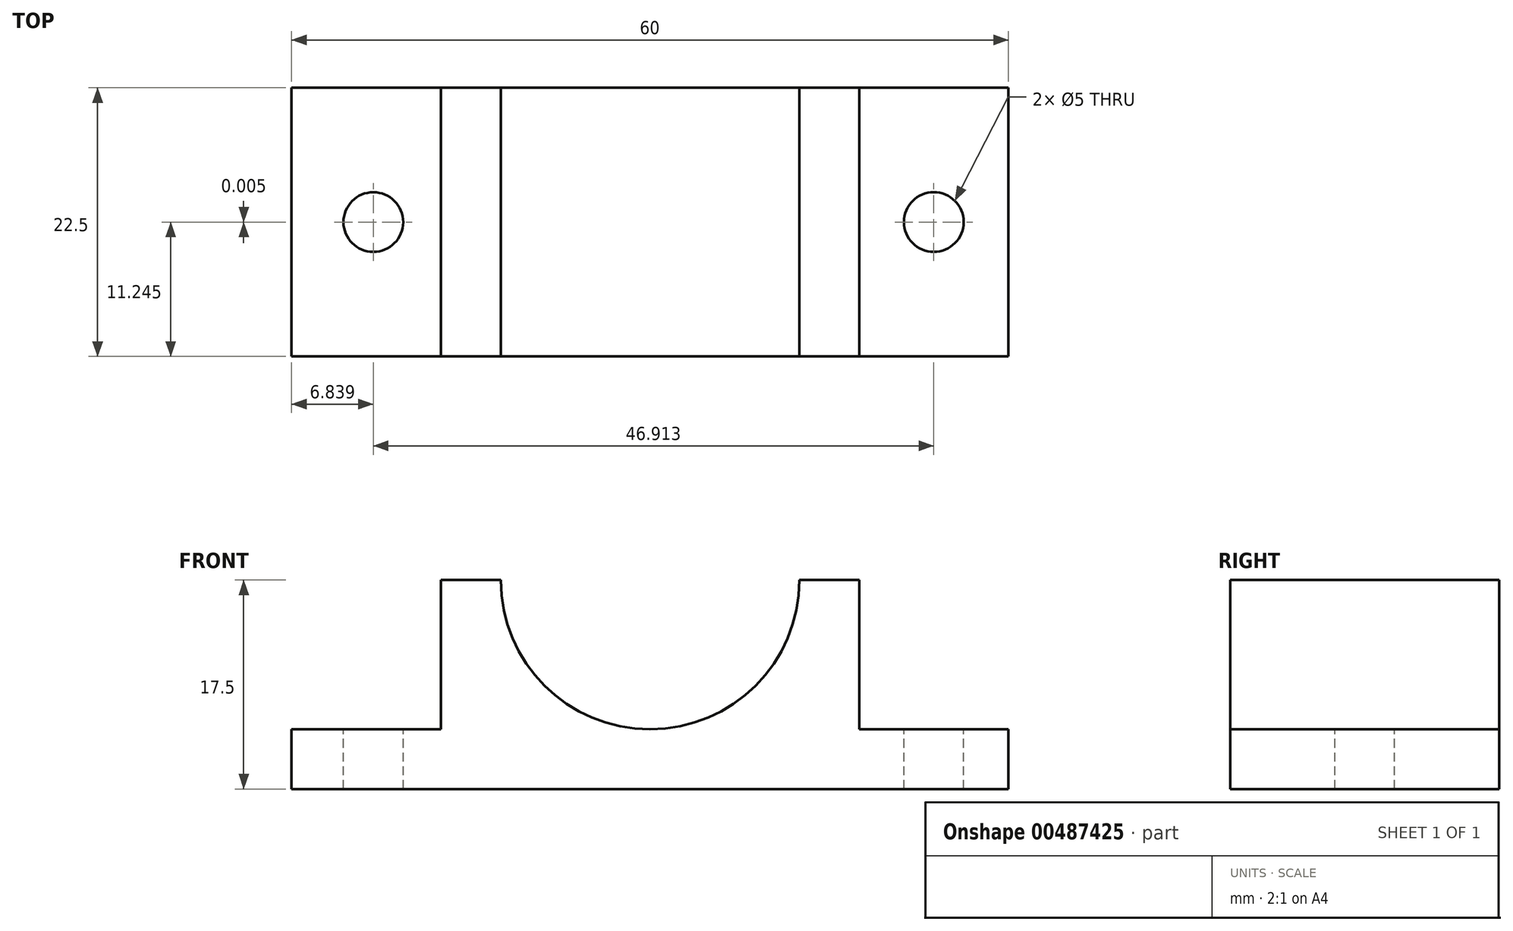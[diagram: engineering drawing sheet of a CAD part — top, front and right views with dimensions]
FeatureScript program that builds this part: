
annotation { "Feature Type Name" : "Feature", "Feature Type Description" : "" }
export const myFeature = defineFeature(function(context is Context, id is Id, definition is map)
    precondition{}
    {
        {
            var Q0;
            Q0=qCreatedBy(makeId("Front.planeOp"),FACE);
            var sketch = newSketch(context, id + "F0", { "sketchPlane" : qUnion([Q0])});
            skLineSegment(sketch, "E0", {"start": v(-13.28, 0) * mm, "end": v(46.72, 0) * mm});
            skLineSegment(sketch, "E1", {"start": v(46.72, 0) * mm, "end": v(46.72, 5) * mm});
            skLineSegment(sketch, "E2", {"start": v(-13.28, 5) * mm, "end": v(-13.28, 0) * mm});
            skLineSegment(sketch, "E3", {"start": v(-13.28, 5) * mm, "end": v(-0.78, 5) * mm});
            skLineSegment(sketch, "E4", {"start": v(-0.78, 5) * mm, "end": v(-0.78, 17.5) * mm});
            skLineSegment(sketch, "E5", {"start": v(34.22, 17.5) * mm, "end": v(34.22, 5) * mm});
            skLineSegment(sketch, "E6", {"start": v(34.22, 5) * mm, "end": v(46.72, 5) * mm});
            skLineSegment(sketch, "E7", {"start": v(-0.78, 17.5) * mm, "end": v(4.22, 17.5) * mm});
            skLineSegment(sketch, "E8", {"start": v(29.22, 17.5) * mm, "end": v(34.22, 17.5) * mm});
            skArc(sketch, "E9", {"start": v(4.22, 17.5) * mm, "mid": v(16.72, 5) * mm, "end": v(29.22, 17.5) * mm});
            skSolve(sketch);
        }
        {
            var Q0;
            Q0=makeQuery(id+"F0.imprint","IMPRINT",FACE,{"disambiguationData":[TD([[makeQuery(id+"F0.imprint","IMPRINT",EDGE,{"derivedFrom":sQuery(id+"F0.wireOp",EDGE,"E0")}),1.0]])]});
            extrude(context, id + "F1", {"entities" : qUnion([Q0]), "depth" : 22.5 * mm});
        }
        {
            var Q0;
            Q0=makeQuery(id+"F1.opExtrude","SWEPT_FACE",FACE,{"disambiguationData":[OSD([sQuery(id+"F0.wireOp",EDGE,"E6")])]});
            var sketch = newSketch(context, id + "F2", { "sketchPlane" : qUnion([Q0])});
            skCircle(sketch, "E10", {"center": v(40.47, -11.25) * mm, "radius": 2.5 * mm});
            skCircle(sketch, "E11", {"center": v(-6.44, -11.26) * mm, "radius": 2.5 * mm});
            skSolve(sketch);
        }
        {
            var Q0;
            Q0=makeQuery(id+"F2.imprint","IMPRINT",FACE,{"disambiguationData":[TD([[makeQuery(id+"F2.imprint","IMPRINT",EDGE,{"derivedFrom":sQuery(id+"F2.wireOp",EDGE,"E10")}),1.0]])]});
            extrude(context, id + "F3", {"entities" : qUnion([Q0]), "operationType" : NewBodyOperationType.REMOVE, "endBound" : BoundingType.THROUGH_ALL, "oppositeDirection" : true, "depth" : 25.4 * mm});
        }
        {
            var Q0;
            Q0=makeQuery(id+"F2.imprint","IMPRINT",FACE,{"disambiguationData":[TD([[makeQuery(id+"F2.imprint","IMPRINT",EDGE,{"derivedFrom":sQuery(id+"F2.wireOp",EDGE,"E11")}),1.0]])]});
            extrude(context, id + "F4", {"entities" : qUnion([Q0]), "operationType" : NewBodyOperationType.REMOVE, "endBound" : BoundingType.THROUGH_ALL, "oppositeDirection" : true, "depth" : 25.4 * mm});
        }
    });
